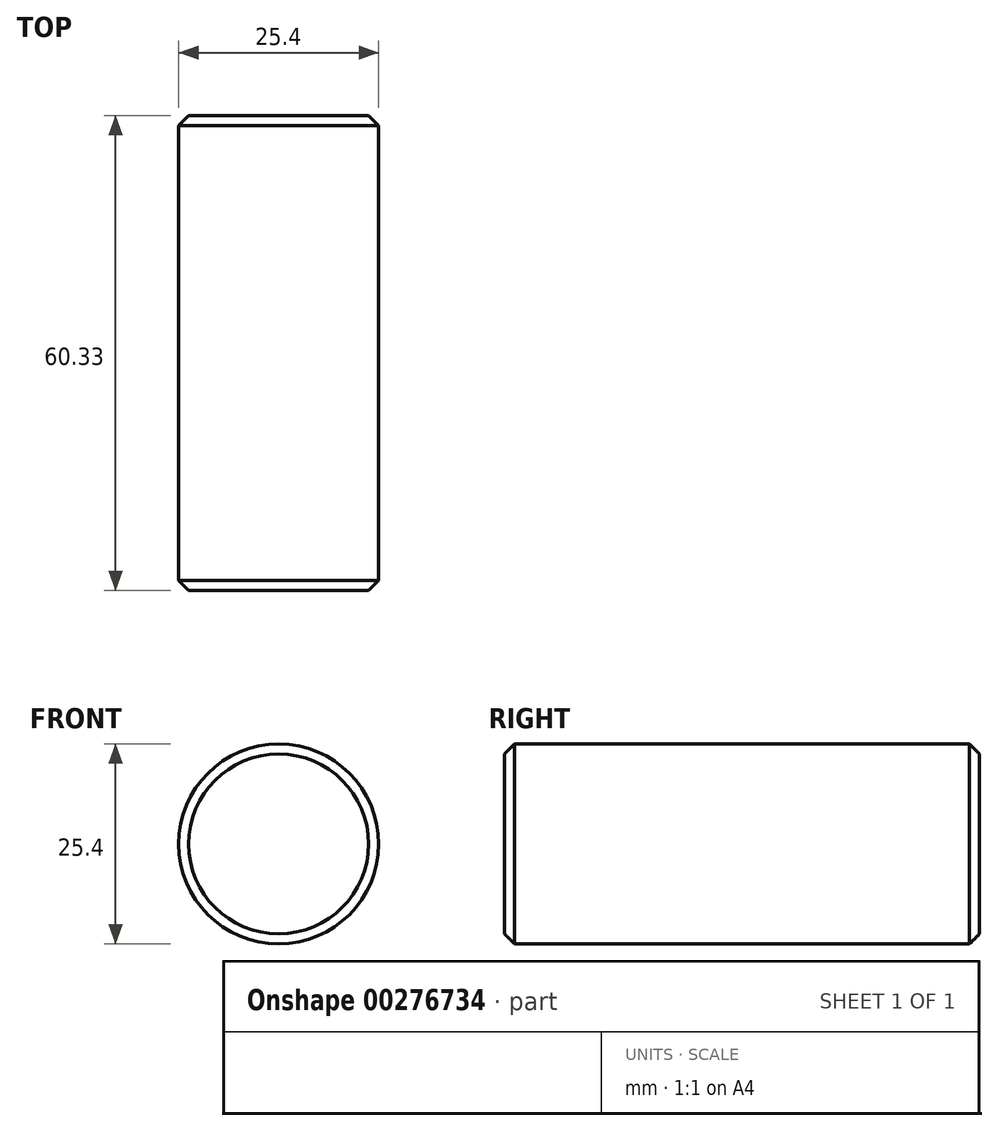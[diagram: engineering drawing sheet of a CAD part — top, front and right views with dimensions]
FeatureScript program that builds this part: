
annotation { "Feature Type Name" : "Feature", "Feature Type Description" : "" }
export const myFeature = defineFeature(function(context is Context, id is Id, definition is map)
    precondition{}
    {
        {
            var Q0;
            Q0=qCreatedBy(makeId("Front.planeOp"),FACE);
            var sketch = newSketch(context, id + "F0", { "sketchPlane" : qUnion([Q0])});
            skCircle(sketch, "E0", {"center": v(0, 0) * mm, "radius": 12.7 * mm});
            skSolve(sketch);
        }
        {
            var Q0;
            Q0 = qSketchRegion(id + "F0", true);
            extrude(context, id + "F1", {"entities" : qUnion([Q0]), "oppositeDirection" : true, "depth" : 60.32 * mm});
        }
        {
            var Q0;
            Q0=makeQuery(id+"F1.opExtrude","CAP_EDGE",EDGE,{"disambiguationData":[OSD([sQuery(id+"F0.wireOp",EDGE,"E0")])],"isStart":true});
            var Q1;
            Q1=makeQuery(id+"F1.opExtrude","CAP_EDGE",EDGE,{"disambiguationData":[OSD([sQuery(id+"F0.wireOp",EDGE,"E0")])],"isStart":false});
            chamfer(context, id + "F2", {"entities" : qUnion([Q0, Q1]), "chamferType" : ChamferType.OFFSET_ANGLE, "width" : 1.27 * mm, "oppositeDirection" : false, "angle" : 45 * degree, "tangentPropagation" : true});
        }
    });
